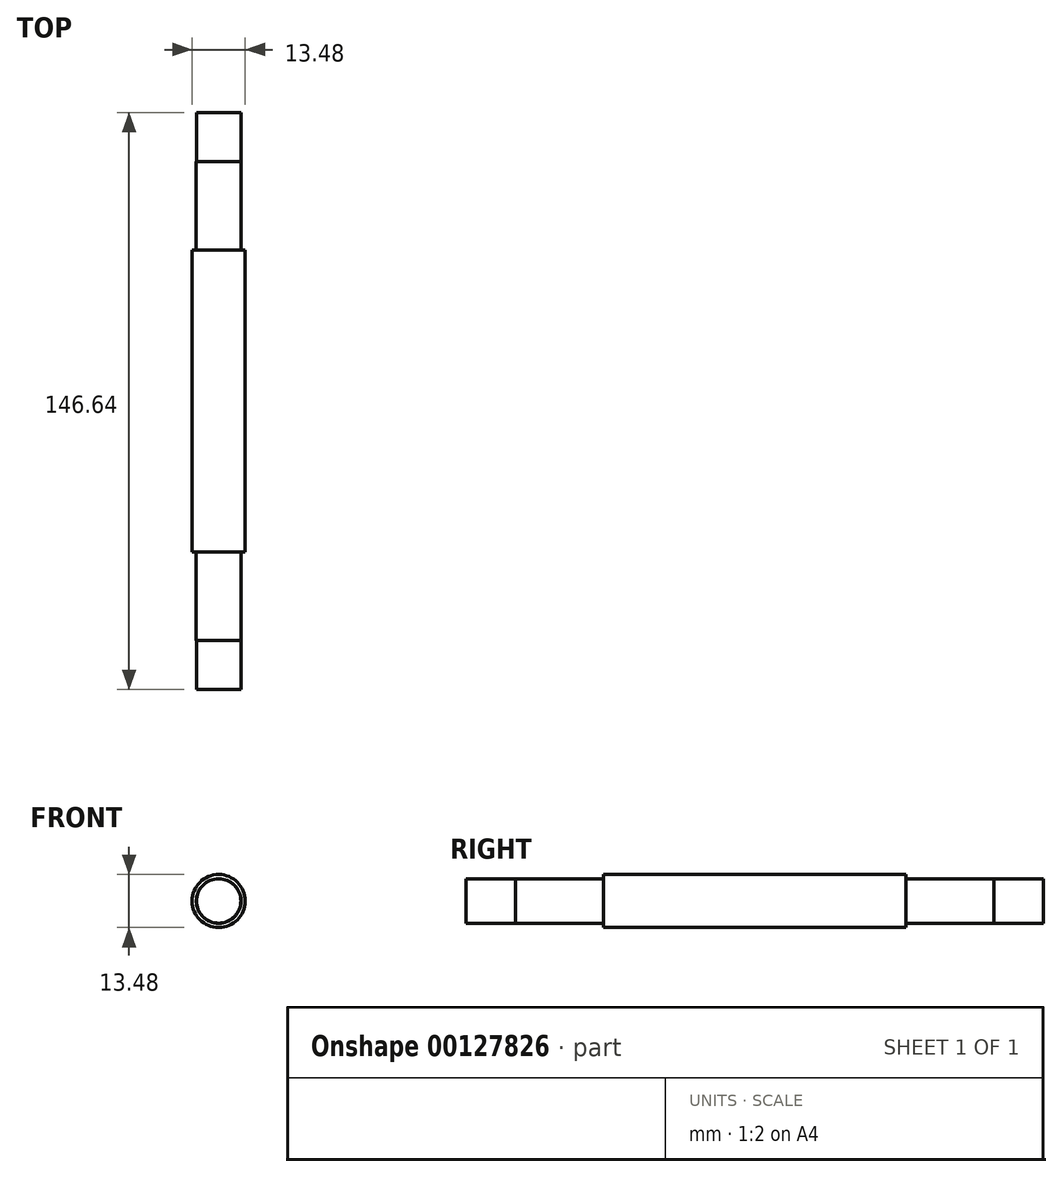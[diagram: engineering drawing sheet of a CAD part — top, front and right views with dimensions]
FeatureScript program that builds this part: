
annotation { "Feature Type Name" : "Feature", "Feature Type Description" : "" }
export const myFeature = defineFeature(function(context is Context, id is Id, definition is map)
    precondition{}
    {
        {
            var Q0;
            Q0=qCreatedBy(makeId("Front.planeOp"),FACE);
            var sketch = newSketch(context, id + "F0", { "sketchPlane" : qUnion([Q0])});
            skCircle(sketch, "E0", {"center": v(0, 0) * mm, "radius": 6.74 * mm});
            skSolve(sketch);
        }
        {
            var Q0;
            Q0 = qSketchRegion(id + "F0", true);
            extrude(context, id + "F1", {"entities" : qUnion([Q0]), "endBound" : BoundingType.SYMMETRIC, "depth" : 76.8 * mm});
        }
        {
            var Q0;
            Q0=makeQuery(id+"F1.opExtrude","CAP_FACE",FACE,{"disambiguationData":[OSD([sQuery(id+"F0.wireOp",EDGE,"E0")])],"isStart":false});
            var sketch = newSketch(context, id + "F2", { "sketchPlane" : qUnion([Q0])});
            skCircle(sketch, "E1", {"center": v(0, 0) * mm, "radius": 5.68 * mm});
            skSolve(sketch);
        }
        {
            var Q0;
            Q0 = qSketchRegion(id + "F2", true);
            extrude(context, id + "F3", {"entities" : qUnion([Q0]), "operationType" : NewBodyOperationType.ADD, "depth" : 22.42 * mm});
        }
        {
            var Q0;
            Q0=makeQuery(id+"F3.opExtrude","CAP_FACE",FACE,{"disambiguationData":[OSD([sQuery(id+"F2.wireOp",EDGE,"E1")])],"isStart":false});
            var sketch = newSketch(context, id + "F4", { "sketchPlane" : qUnion([Q0])});
            skCircle(sketch, "E2", {"center": v(0, 0) * mm, "radius": 5.62 * mm});
            skSolve(sketch);
        }
        {
            var Q0;
            Q0 = qSketchRegion(id + "F4", true);
            extrude(context, id + "F5", {"entities" : qUnion([Q0]), "operationType" : NewBodyOperationType.ADD, "depth" : 12.5 * mm});
        }
        {
            var Q0;
            Q0=makeQuery(id+"F1.opExtrude","CAP_FACE",FACE,{"disambiguationData":[OSD([sQuery(id+"F0.wireOp",EDGE,"E0")])],"isStart":true});
            var sketch = newSketch(context, id + "F6", { "sketchPlane" : qUnion([Q0])});
            skCircle(sketch, "E3", {"center": v(0, 0) * mm, "radius": 5.68 * mm});
            skSolve(sketch);
        }
        {
            var Q0;
            Q0 = qSketchRegion(id + "F6", true);
            extrude(context, id + "F7", {"entities" : qUnion([Q0]), "operationType" : NewBodyOperationType.ADD, "depth" : 22.42 * mm});
        }
        {
            var Q0;
            Q0=makeQuery(id+"F7.opExtrude","CAP_FACE",FACE,{"disambiguationData":[OSD([sQuery(id+"F6.wireOp",EDGE,"E3")])],"isStart":false});
            var sketch = newSketch(context, id + "F8", { "sketchPlane" : qUnion([Q0])});
            skCircle(sketch, "E4", {"center": v(0, 0) * mm, "radius": 5.62 * mm});
            skSolve(sketch);
        }
        {
            var Q0;
            Q0 = qSketchRegion(id + "F8", true);
            extrude(context, id + "F9", {"entities" : qUnion([Q0]), "operationType" : NewBodyOperationType.ADD, "depth" : 12.5 * mm});
        }
    });
